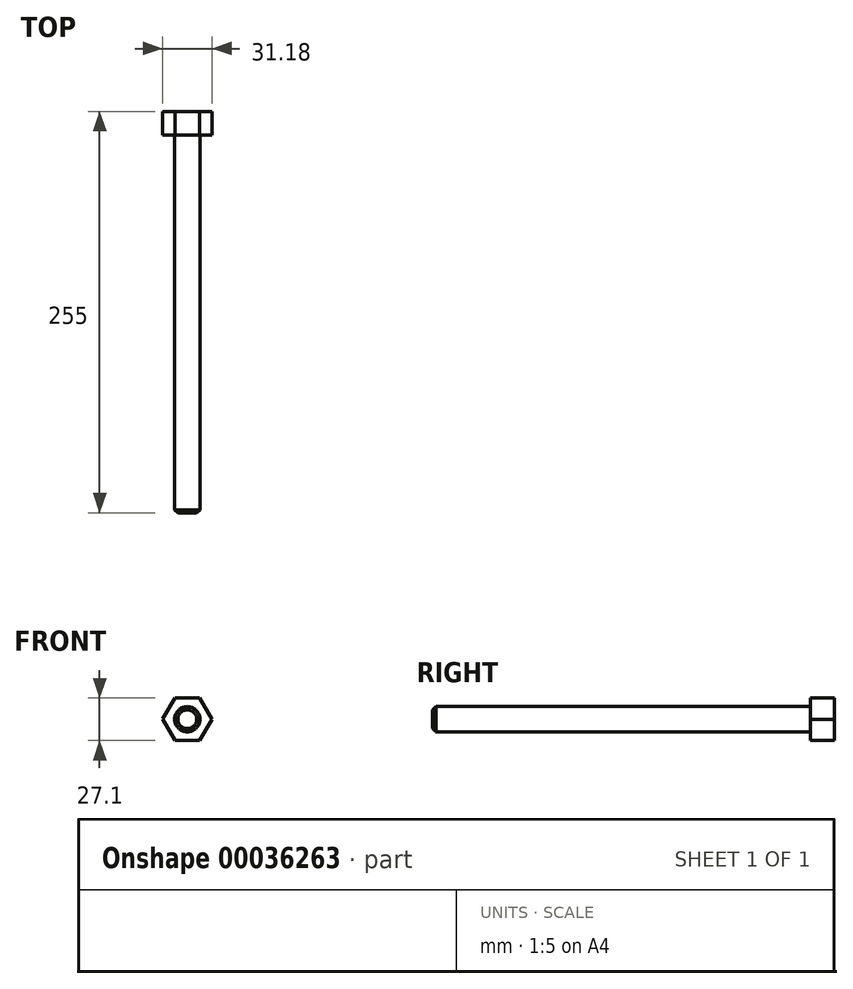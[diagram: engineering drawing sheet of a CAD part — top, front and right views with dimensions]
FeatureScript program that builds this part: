
annotation { "Feature Type Name" : "Feature", "Feature Type Description" : "" }
export const myFeature = defineFeature(function(context is Context, id is Id, definition is map)
    precondition{}
    {
        {
            var Q0;
            Q0=qCreatedBy(makeId("Front.planeOp"),FACE);
            var sketch = newSketch(context, id + "F0", { "sketchPlane" : qUnion([Q0])});
            skCircle(sketch, "E0.cCircle", {"center": v(0, 0) * mm, "radius": 15.59 * mm, "construction": true});
            skLineSegment(sketch, "E0.0", {"start": v(-7.88, -13.45) * mm, "end": v(-15.59, 0.1) * mm});
            skLineSegment(sketch, "E0.1", {"start": v(-15.59, 0.1) * mm, "end": v(-7.7, 13.55) * mm});
            skLineSegment(sketch, "E0.2", {"start": v(-7.7, 13.55) * mm, "end": v(7.88, 13.45) * mm});
            skLineSegment(sketch, "E0.3", {"start": v(7.88, 13.45) * mm, "end": v(15.59, -0.1) * mm});
            skLineSegment(sketch, "E0.4", {"start": v(15.59, -0.1) * mm, "end": v(7.7, -13.55) * mm});
            skLineSegment(sketch, "E0.5", {"start": v(7.7, -13.55) * mm, "end": v(-7.88, -13.45) * mm});
            skSolve(sketch);
        }
        {
            var Q0;
            Q0 = qSketchRegion(id + "F0", true);
            extrude(context, id + "F1", {"entities" : qUnion([Q0]), "oppositeDirection" : true, "depth" : 15 * mm});
        }
        {
            var Q0;
            Q0=makeQuery(id+"F1.opExtrude","CAP_FACE",FACE,{"disambiguationData":[OSD([sQuery(id+"F0.wireOp",EDGE,"E0.0"),sQuery(id+"F0.wireOp",EDGE,"E0.1"),sQuery(id+"F0.wireOp",EDGE,"E0.2"),sQuery(id+"F0.wireOp",EDGE,"E0.3"),sQuery(id+"F0.wireOp",EDGE,"E0.4"),sQuery(id+"F0.wireOp",EDGE,"E0.5")])],"isStart":true});
            var sketch = newSketch(context, id + "F2", { "sketchPlane" : qUnion([Q0])});
            skCircle(sketch, "E1", {"center": v(0, 0) * mm, "radius": 8 * mm});
            skSolve(sketch);
        }
        {
            var Q0;
            Q0 = qSketchRegion(id + "F2", true);
            extrude(context, id + "F3", {"entities" : qUnion([Q0]), "operationType" : NewBodyOperationType.ADD, "depth" : 240 * mm});
        }
        {
            var Q0;
            Q0=makeQuery(id+"F3.opExtrude","CAP_EDGE",EDGE,{"disambiguationData":[OSD([sQuery(id+"F2.wireOp",EDGE,"E1")])],"isStart":false});
            chamfer(context, id + "F4", {"entities" : qUnion([Q0]), "width" : 2 * mm, "tangentPropagation" : true});
        }
    });
